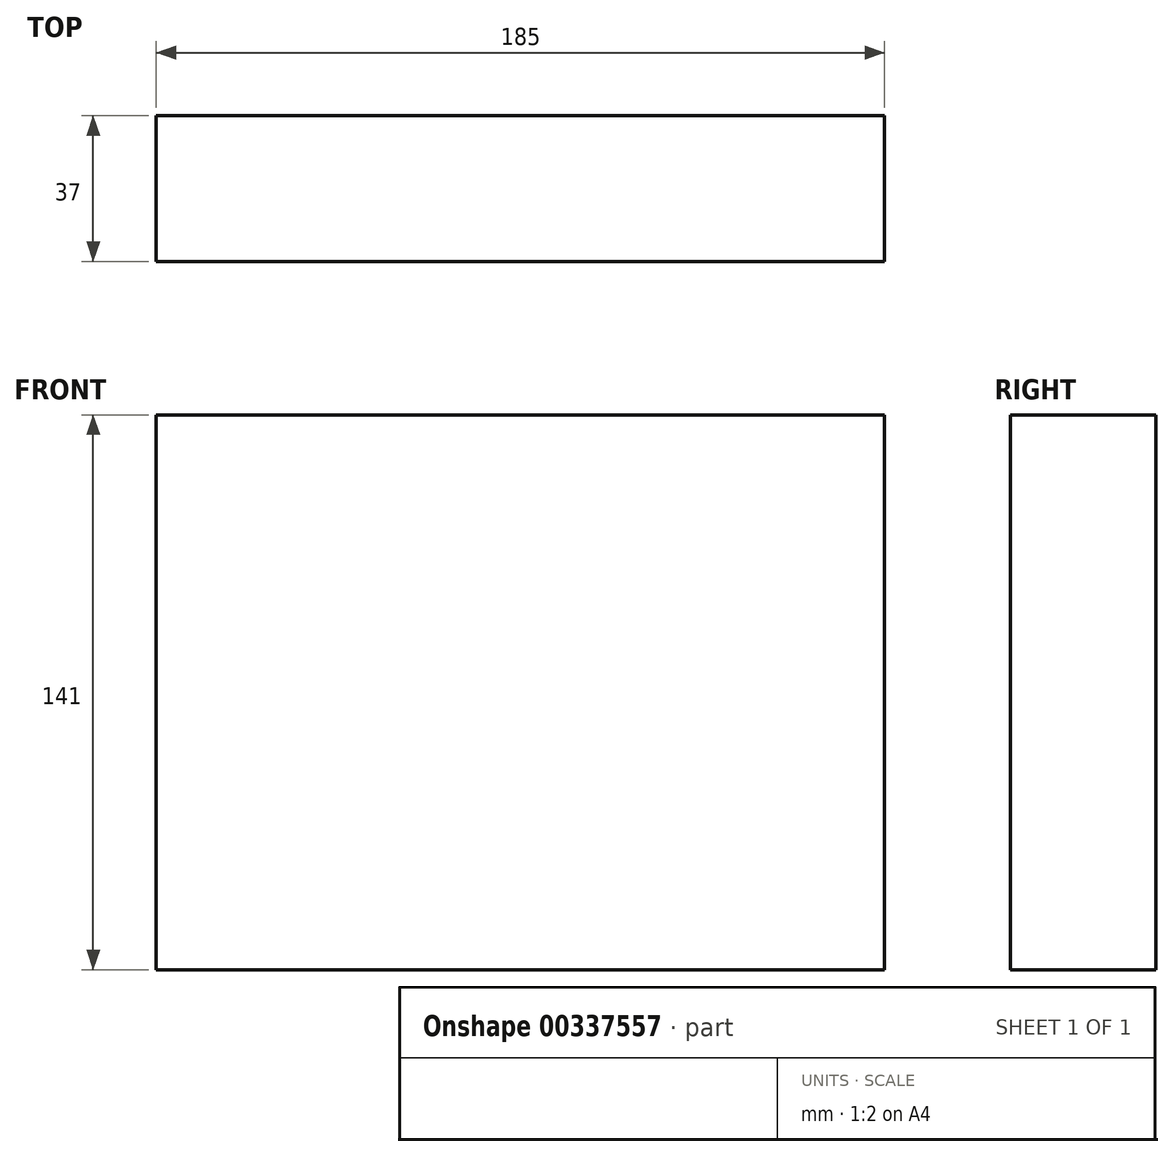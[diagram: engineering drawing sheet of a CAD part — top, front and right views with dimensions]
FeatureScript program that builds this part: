
annotation { "Feature Type Name" : "Feature", "Feature Type Description" : "" }
export const myFeature = defineFeature(function(context is Context, id is Id, definition is map)
    precondition{}
    {
        {
            var Q0;
            Q0=qCreatedBy(makeId("Front.planeOp"),FACE);
            var sketch = newSketch(context, id + "F0", { "sketchPlane" : qUnion([Q0])});
            skLineSegment(sketch, "E0.bottom", {"start": v(0, 0) * mm, "end": v(185, 0) * mm});
            skLineSegment(sketch, "E0.top", {"start": v(0, 141) * mm, "end": v(185, 141) * mm});
            skLineSegment(sketch, "E0.left", {"start": v(0, 0) * mm, "end": v(0, 141) * mm});
            skLineSegment(sketch, "E0.right", {"start": v(185, 0) * mm, "end": v(185, 141) * mm});
            skSolve(sketch);
        }
        {
            var Q0;
            Q0 = qSketchRegion(id + "F0", true);
            extrude(context, id + "F1", {"entities" : qUnion([Q0]), "depth" : (18.5 * 2) * mm});
        }
    });
